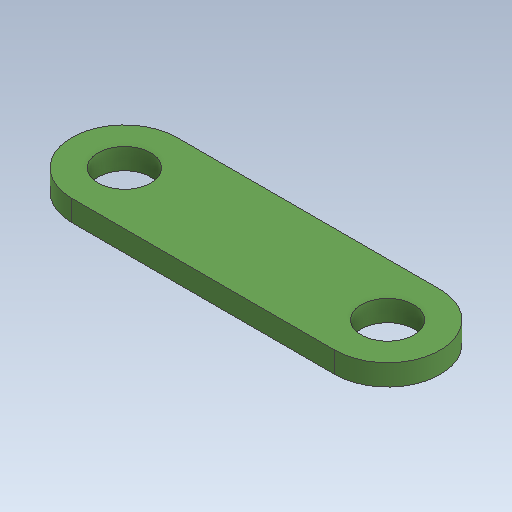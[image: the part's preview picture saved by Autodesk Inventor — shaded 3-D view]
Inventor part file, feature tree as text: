
AUTODESK INVENTOR PART (.ipt)
format: ipt  version: 2020.1 (Build 241239000, 239)  size: 120,832 bytes
history: native  units: in
note: dims shown in document units (in); Inventor stores cm internally (conversion verified against a paired STEP export)
features: extrude x1, sketch x1
ambient origin geometry x8: Origin, YZ Plane, XZ Plane, XY Plane, X Axis, Y Axis, Z Axis, Center Point
bodies: Solid1 (feature_tree)
feature tree (2):
  extrude  "Extrusion1"  Depth=10.0in
  sketch  "Sketch1"  dims[d0=25.0in d1=10.0in d2=5.0in d3=5.0in d4=2.0in d5=0.0in]
